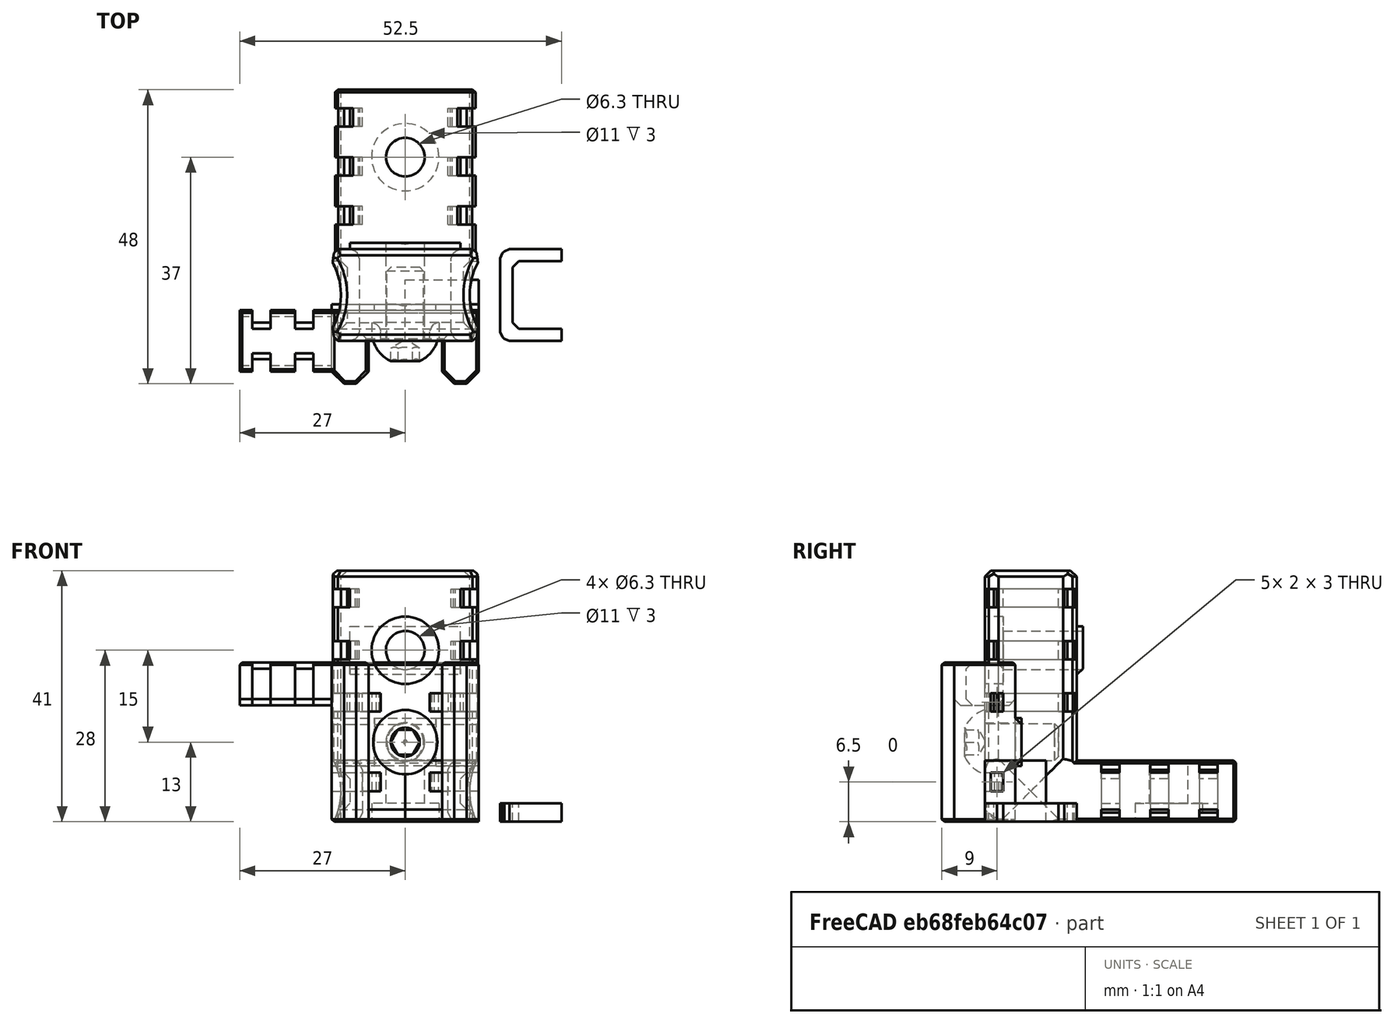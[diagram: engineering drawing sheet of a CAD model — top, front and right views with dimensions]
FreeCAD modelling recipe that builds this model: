
FCSTD DOCUMENT  (FreeCAD 0.19R24291 (Git))
Label: back-cable-mounter
License: Other
LicenseURL: GPL3
objects: Part::Box×19, Part::MultiFuse×19, Part::Chamfer×17, Part::Feature×15, Part::Cut×9, Part::Cylinder×5, Part::FeaturePython×1, App::Part×1, Part::Refine×1
note: 86 computed .brp shape members not serialized (recipe doc carries the construction recipe); baked Part::Feature solids carry a one-line shape summary decoded from their .brp

FEATURE [Part::Box] Box  label="Cube"
  AttacherType = Attacher::AttachEngine3D
  Height = 10
  Length = 12
  Width = 10
FEATURE [Part::Cylinder] Cylinder
  Angle = 360
  AttacherType = Attacher::AttachEngine3D
  Height = 29
  Placement = pos=(0,3e-15,13) rot=(-1,0,0;1.5708rad)
  Radius = 3.15
FEATURE [Part::Cylinder] Cylinder001
  Angle = 360
  AttacherType = Attacher::AttachEngine3D
  Height = 20
  Placement = pos=(0,2.9e-15,13) rot=(1,0,0;1.5708rad)
  Radius = 5.5
FEATURE [Part::MultiFuse] Fusion  label="m6-bolt"
  Placement = pos=(0,3,15) rot=(0,0,1;0rad)
  Shapes = -> [Cylinder001,Cylinder]
FEATURE [Part::Box] Box001  label="Cube001"
  AttacherType = Attacher::AttachEngine3D
  Height = 39
  Length = 26
  Placement = pos=(-13,0,2) rot=(0,0,1;0rad)
  Width = 15
FEATURE [Part::Cylinder] Cylinder002
  Angle = 360
  AttacherType = Attacher::AttachEngine3D
  Height = 41
  Placement = pos=(21.5,7.5,0) rot=(0,0,1;0rad)
  Radius = 11
FEATURE [Part::Cylinder] Cylinder003
  Angle = 360
  AttacherType = Attacher::AttachEngine3D
  Height = 41
  Placement = pos=(-21.5,7.5,0) rot=(0,0,1;0rad)
  Radius = 11
FEATURE [Part::Box] Box002  label="Cube002"
  AttacherType = Attacher::AttachEngine3D
  Height = 3
  Length = 10
  Placement = pos=(15.5,0,0) rot=(0,0,1;0rad)
  Width = 2
FEATURE [Part::Box] Box003  label="Cube003"
  AttacherType = Attacher::AttachEngine3D
  Height = 3
  Length = 10
  Placement = pos=(15.5,13,0) rot=(0,0,1;0rad)
  Width = 2
FEATURE [Part::Box] Box004  label="Cube004"
  AttacherType = Attacher::AttachEngine3D
  Height = 3
  Length = 2
  Placement = pos=(15.5,2,0) rot=(0,0,1;0rad)
  Width = 11
FEATURE [Part::MultiFuse] Fusion002
  Shapes = -> [Box004,Box003,Box002]
FEATURE [Part::Chamfer] Chamfer002
  Base = -> Fusion002
  Edges = 4 edges r=1: [Edge5,Edge12,Edge27,Edge28]
FEATURE [Part::Chamfer] Chamfer003
  Base = -> Chamfer002
  Edges = 4 edges r=0.5: [Edge2,Edge12,Edge31,Edge45]
FEATURE [Part::Feature] Chamfer003001
  Placement = pos=(-8,0,0) rot=(0,0,1;0rad)
  shape: bbox 10 x 15 x 3 mm, 24 faces (baked)
FEATURE [Part::Feature] Chamfer003002
  Placement = pos=(8,15,0) rot=(0,0,1;3.14159rad)
  shape: bbox 10 x 15 x 3 mm, 24 faces (baked)
FEATURE [Part::MultiFuse] Fusion003
  Placement = pos=(0,0,3) rot=(0,0,1;0rad)
  Shapes = -> [Chamfer003002,Chamfer003001]
FEATURE [Part::Feature] Fusion003001
  Placement = pos=(0,0,20) rot=(0,0,1;0rad)
  shape: bbox 35 x 15 x 3 mm, 48 faces, 2 solids (baked)
FEATURE [Part::Feature] Fusion003002
  Placement = pos=(0,0,11.5) rot=(0,0,1;0rad)
  shape: bbox 35 x 15 x 3 mm, 48 faces, 2 solids (baked)
FEATURE [Part::MultiFuse] Fusion003003
  Placement = pos=(0,0,15) rot=(0,0,1;0rad)
  Shapes = -> [Fusion003002,Fusion003001,Fusion003]
FEATURE [Part::Box] Box005  label="Cube005"
  AttacherType = Attacher::AttachEngine3D
  Height = 7.8
  Length = 18
  Placement = pos=(-9,15,24.1) rot=(0,0,1;0rad)
  Width = 1
FEATURE [Part::Feature] Fusion003004  label="m6-bolt001"
  Placement = pos=(0,43,3) rot=(1,0,0;1.5708rad)
  shape: bbox 11 x 11 x 49 mm, 5 faces (baked)
FEATURE [Part::Box] Box006  label="Cube006"
  AttacherType = Attacher::AttachEngine3D
  Height = 10
  Length = 26
  Placement = pos=(-13,0,0) rot=(0,0,1;0rad)
  Width = 41
FEATURE [Part::Chamfer] Chamfer003003
  Base = -> Box006
  Edges = 7 edges r=2: [Edge1,Edge2,Edge4,Edge5,Edge6,Edge8,Edge9]
FEATURE [Part::Chamfer] Chamfer
  Base = -> Box001
  Edges = 4 edges r=2: [Edge1,Edge3,Edge5,Edge7]
FEATURE [Part::MultiFuse] Fusion003005004
  Shapes = -> [Chamfer,Chamfer003003]
FEATURE [Part::Chamfer] Chamfer003004
  Base = -> Box005
  Edges = 1 edges r=0.9: [Edge11]
FEATURE [Part::MultiFuse] Fusion003005005
  Shapes = -> [Cylinder002,Cylinder003]
FEATURE [Part::Feature] Fusion003005005001
  Placement = pos=(0,3e-15,12.5) rot=(-1,0,0;1.5708rad)
  shape: bbox 65 x 41 x 22 mm, 6 faces, 2 solids (baked)
FEATURE [Part::MultiFuse] Fusion003005005002
  Shapes = -> [Fusion003005005,Fusion003005005001]
FEATURE [Part::Cut] Cut
  Base = -> Fusion003005004
  Tool = -> Fusion003005005002
FEATURE [Part::Chamfer] Chamfer003005
  Base = -> Cut
  Edges = 9 edges r=0.4: [Edge37,Edge40,Edge41,Edge43,Edge45,Edge62,Edge63,Edge64,Edge65]
FEATURE [Part::Chamfer] Chamfer003006
  Base = -> Chamfer003005
  Edges = 9 edges r=1: [Edge13,Edge19,Edge34,Edge35,Edge36,Edge37,Edge38,Edge39,Edge40]
FEATURE [Part::MultiFuse] Fusion003005005003
  Shapes = -> [Chamfer003006,Chamfer003004]
FEATURE [Part::Box] Box007  label="Cube007"
  AttacherType = Attacher::AttachEngine3D
  Height = 10
  Length = 2
  Placement = pos=(7,35,0) rot=(0,0,1;0rad)
  Width = 3
FEATURE [Part::Chamfer] Chamfer003007
  Base = -> Fusion003005005003
  Edges = 4 edges r=1: [Edge4,Edge26,Edge50,Edge67]
FEATURE [Part::Cut] Cut001
  Base = -> Chamfer003007
  Tool = -> Fusion003003
FEATURE [Part::Cut] Cut002
  Base = -> Cut001
  Tool = -> Fusion
FEATURE [Part::Cut] Cut003
  Base = -> Cut002
  Tool = -> Fusion003004
FEATURE [Part::Box] Box008  label="Cube008"
  AttacherType = Attacher::AttachEngine3D
  Height = 2
  Length = 10
  Placement = pos=(7,35,0) rot=(0,0,1;0rad)
  Width = 3
FEATURE [Part::Box] Box009  label="Cube009"
  AttacherType = Attacher::AttachEngine3D
  Height = 2
  Length = 10
  Placement = pos=(7,35,8) rot=(0,0,1;0rad)
  Width = 3
FEATURE [Part::MultiFuse] Fusion003005005004
  Shapes = -> [Box009,Box007,Box008]
FEATURE [Part::Chamfer] Chamfer003008
  Base = -> Fusion003005005004
  Edges = 4 edges r=1: [Edge2,Edge28,Edge31,Edge32]
FEATURE [Part::Chamfer] Chamfer003009
  Base = -> Chamfer003008
  Edges = 4 edges r=0.5: [Edge4,Edge10,Edge31,Edge56]
FEATURE [Part::Feature] Chamfer003009001
  Placement = pos=(0,-8,0) rot=(0,0,1;0rad)
  shape: bbox 10 x 3 x 10 mm, 30 faces (baked)
FEATURE [Part::Feature] Chamfer003009002
  Placement = pos=(0,-16,0) rot=(0,0,1;0rad)
  shape: bbox 10 x 3 x 10 mm, 30 faces (baked)
FEATURE [Part::MultiFuse] Fusion003005005005
  Shapes = -> [Chamfer003009002,Chamfer003009,Chamfer003009001]
FEATURE [Part::Feature] Fusion003005005005001
  Placement = pos=(-1e-15,0,10) rot=(0,1,0;3.14159rad)
  shape: bbox 10 x 19 x 10 mm, 90 faces, 3 solids (baked)
FEATURE [Part::MultiFuse] Fusion003005005005002
  Shapes = -> [Fusion003005005005001,Fusion003005005005]
FEATURE [Part::Cut] Cut004
  Base = -> Cut003
  Tool = -> Fusion003005005005002
FEATURE [Part::Box] Box010  label="Cube010"
  AttacherType = Attacher::AttachEngine3D
  Height = 26
  Length = 24
  Placement = pos=(-12,0,0) rot=(0,0,1;0rad)
  Width = 5
FEATURE [Part::Cylinder] Cylinder004
  Angle = 360
  AttacherType = Attacher::AttachEngine3D
  Height = 10
  Placement = pos=(0,0,13) rot=(-1,0,0;1.5708rad)
  Radius = 3.15
FEATURE [Part::Box] Box011  label="Cube011"
  AttacherType = Attacher::AttachEngine3D
  Height = 26
  Length = 6
  Placement = pos=(-12,-7,0) rot=(0,0,1;0rad)
  Width = 8
FEATURE [Part::Box] Box012  label="Cube012"
  AttacherType = Attacher::AttachEngine3D
  Height = 7.8
  Length = 24
  Placement = pos=(-12,4,9.1) rot=(0,0,1;0rad)
  Width = 2
FEATURE [Part::Box] Box013  label="Cube013"
  AttacherType = Attacher::AttachEngine3D
  Height = 3
  Length = 10
  Width = 2
FEATURE [Part::Box] Box014  label="Cube014"
  AttacherType = Attacher::AttachEngine3D
  Height = 3
  Length = 2
  Placement = pos=(8,-10,0) rot=(0,0,1;0rad)
  Width = 10
FEATURE [Part::MultiFuse] Fusion003005005005005
  Shapes = -> [Box014,Box013]
FEATURE [Part::Chamfer] Chamfer003009003003
  Base = -> Fusion003005005005005
  Edges = 2 edges r=1: [Edge3,Edge23]
FEATURE [Part::Chamfer] Chamfer003009003004
  Base = -> Chamfer003009003003
  Edges = 2 edges r=0.4: [Edge30,Edge31]
  Placement = pos=(-14,1,5) rot=(0,0,1;0rad)
FEATURE [Part::Feature] Chamfer003009003004001
  Placement = pos=(-14,1,18) rot=(0,0,1;0rad)
  shape: bbox 10 x 12 x 3 mm, 15 faces (baked)
FEATURE [Part::MultiFuse] Fusion003005005005006
  Shapes = -> [Chamfer003009003004,Chamfer003009003004001]
FEATURE [Part::Feature] Fusion003005005005006001
  Placement = pos=(-3e-15,0,26) rot=(0,1,0;3.14159rad)
  shape: bbox 10 x 12 x 16 mm, 30 faces, 2 solids (baked)
FEATURE [Part::MultiFuse] Fusion003005005005006002
  Shapes = -> [Fusion003005005005006001,Fusion003005005005006]
FEATURE [Part::Chamfer] Chamfer003009003004002
  Base = -> Box011
  Edges = 2 edges r=2: [Edge1,Edge5]
FEATURE [Part::Feature] Chamfer003009003004002001
  Placement = pos=(18,0,0) rot=(0,0,1;0rad)
  shape: bbox 6 x 8 x 26 mm, 8 faces (baked)
FEATURE [Part::MultiFuse] Fusion003005005005006003
  Shapes = -> [Chamfer003009003004002001,Box010,Chamfer003009003004002]
FEATURE [Part::Feature] Chamfer003009003004002002001  label="mounter"
  shape: bbox 24 x 13 x 26 mm, 79 faces (baked)
FEATURE [Part::FeaturePython] Screw  label="M6x12-Screw"  # Fasteners workbench fastener (typed FeaturePython)
  Placement = pos=(0,0,13) rot=(1,0,0;1.5708rad)
  baseObject = -> Chamfer003009003004002002001 [Edge159]
  diameter = 4
  invert = true
  length = 1
  lengthCustom = 12
  matchOuter = true
  offset = 0
  thread = false
  type = 39
FEATURE [App::Part] Part  label="back-cable-mounter001"
  Group = -> [Chamfer003009003004002002001,Screw]
  Origin = -> Origin
FEATURE [Part::Box] Box015  label="Cube015"
  AttacherType = Attacher::AttachEngine3D
  Height = 7
  Length = 15
  Placement = pos=(-27,-5,19) rot=(0,0,1;0rad)
  Width = 10
FEATURE [Part::Chamfer] Chamfer003009003004002002003
  Base = -> Box012
  Edges = 1 edges r=1: [Edge12]
FEATURE [Part::MultiFuse] Fusion003005005005006004
  Shapes = -> [Chamfer003009003004002002003,Fusion003005005005006003]
FEATURE [Part::Cut] Cut005
  Base = -> Fusion003005005005006004
  Tool = -> Cylinder004
FEATURE [Part::Cut] Cut006
  Base = -> Cut005
  Tool = -> Fusion003005005005006002
FEATURE [Part::Chamfer] Chamfer003009003004002002004
  Base = -> Box015
  Edges = 2 edges r=1: [Edge9,Edge11]
FEATURE [Part::MultiFuse] Fusion003005005005006005
  Shapes = -> [Chamfer003009003004002002004,Cut006]
FEATURE [Part::Box] Box016  label="Cube016"
  AttacherType = Attacher::AttachEngine3D
  Height = 10
  Length = 3
  Placement = pos=(-25,3,17) rot=(0,0,1;0rad)
  Width = 2
FEATURE [Part::Box] Box017  label="Cube017"
  AttacherType = Attacher::AttachEngine3D
  Height = 10
  Length = 3
  Placement = pos=(-18,3,17) rot=(0,0,1;0rad)
  Width = 2
FEATURE [Part::MultiFuse] Fusion003005005005006006
  Shapes = -> [Box016,Box017]
FEATURE [Part::Feature] Fusion003005005005006006001
  Placement = pos=(0,-8,0) rot=(0,0,1;0rad)
  shape: bbox 10 x 2 x 10 mm, 12 faces, 2 solids (baked)
FEATURE [Part::MultiFuse] Fusion003005005005006006002
  Shapes = -> [Fusion003005005005006006001,Fusion003005005005006006]
FEATURE [Part::Refine] Fusion003005005005006005001
  Source = -> Fusion003005005005006005
FEATURE [Part::Chamfer] Chamfer003009003004002002005
  Base = -> Fusion003005005005006005001
  Edges = 25 edges r=0.4: [Edge47,Edge50,Edge59,Edge61,Edge66,Edge67,Edge77,Edge79,Edge92,Edge109,Edge114,Edge122,Edge132,Edge133,Edge134,Edge135,Edge136,Edge137,Edge138,Edge141,Edge143,Edge146,Edge169,Edge170,Edge171]
FEATURE [Part::Cut] Cut007
  Base = -> Chamfer003009003004002002005
  Tool = -> Fusion003005005005006006002
FEATURE [Part::Chamfer] Chamfer003009003004002002006
  Base = -> Cut007
  Edges = 8 edges r=1: [Edge14,Edge18,Edge26,Edge30,Edge47,Edge59,Edge90,Edge102]
FEATURE [Part::Feature] Chamfer003009003004002002007  label="mounter001"
  shape: bbox 24 x 13 x 26 mm, 79 faces (baked)
FEATURE [Part::Box] Box018  label="Cube018"
  AttacherType = Attacher::AttachEngine3D
  Height = 10
  Length = 10
  Placement = pos=(-5,5,7) rot=(0,0,1;0rad)
  Width = 10
FEATURE [Part::Cut] Cut008
  Base = -> Chamfer003009003004002002007
  Tool = -> Box018
